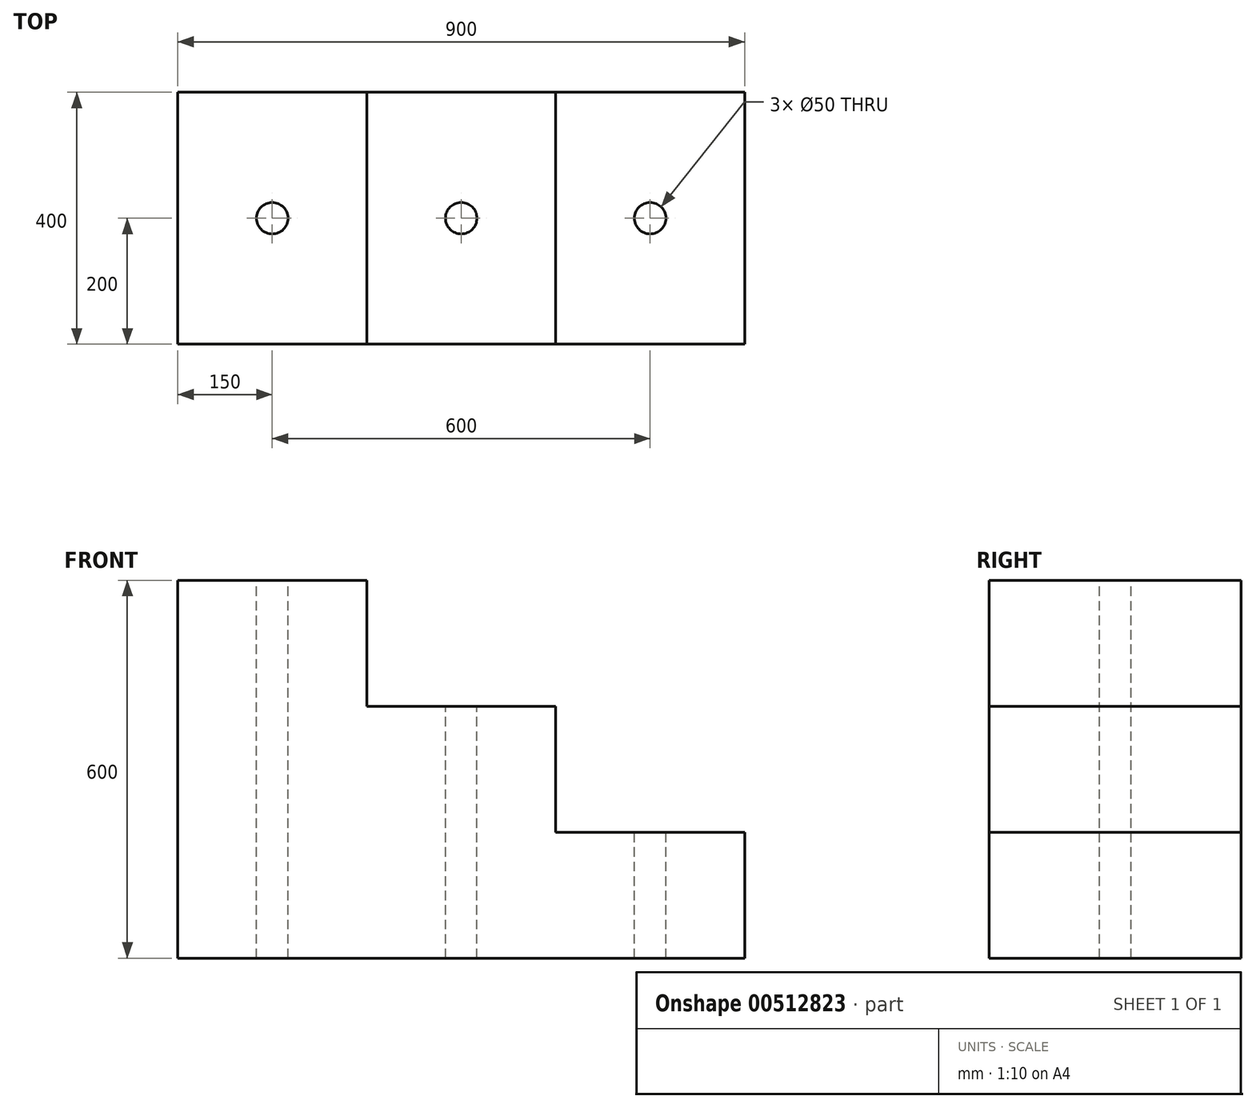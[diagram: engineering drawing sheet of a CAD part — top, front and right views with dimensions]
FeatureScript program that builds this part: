
annotation { "Feature Type Name" : "Feature", "Feature Type Description" : "" }
export const myFeature = defineFeature(function(context is Context, id is Id, definition is map)
    precondition{}
    {
        {
            var Q0;
            Q0=qCreatedBy(makeId("Front.planeOp"),FACE);
            var sketch = newSketch(context, id + "F0", { "sketchPlane" : qUnion([Q0])});
            skLineSegment(sketch, "E0.bottom", {"start": v(-450, 300) * mm, "end": v(-150, 300) * mm});
            skLineSegment(sketch, "E0.top", {"start": v(-450, -300) * mm, "end": v(450, -300) * mm});
            skLineSegment(sketch, "E0.left", {"start": v(-450, 300) * mm, "end": v(-450, -300) * mm});
            skLineSegment(sketch, "E0.right", {"start": v(450, -100) * mm, "end": v(450, -300) * mm});
            skPoint(sketch, "E0.middle", {"position": v(0, 0) * mm});
            skLineSegment(sketch, "E1", {"start": v(-150, 300) * mm, "end": v(-150, 100) * mm});
            skLineSegment(sketch, "E2", {"start": v(-150, 100) * mm, "end": v(150, 100) * mm});
            skPoint(sketch, "E3.end.orphan", {"position": v(150, 0) * mm});
            skLineSegment(sketch, "E4", {"start": v(150, 100) * mm, "end": v(150, -100) * mm});
            skLineSegment(sketch, "E5", {"start": v(150, -100) * mm, "end": v(450, -100) * mm});
            skPoint(sketch, "E6.orphan", {"position": v(450, 300) * mm});
            skSolve(sketch);
        }
        {
            var Q0;
            Q0=makeQuery(id+"F0.imprint","IMPRINT",FACE,{"disambiguationData":[TD([[makeQuery(id+"F0.imprint","IMPRINT",EDGE,{"derivedFrom":sQuery(id+"F0.wireOp",EDGE,"E0.top")}),1.0]])]});
            extrude(context, id + "F1", {"entities" : qUnion([Q0]), "depth" : 400 * mm});
        }
        {
            var Q0;
            Q0=makeQuery(id+"F1.opExtrude","SWEPT_FACE",FACE,{"disambiguationData":[OSD([sQuery(id+"F0.wireOp",EDGE,"E0.bottom")])]});
            var sketch = newSketch(context, id + "F2", { "sketchPlane" : qUnion([Q0])});
            skCircle(sketch, "E7", {"center": v(-300, -200) * mm, "radius": 25 * mm});
            skPoint(sketch, "E7.first.point", {"position": v(-279.89, -214.85) * mm});
            skPoint(sketch, "E7.second.point", {"position": v(-275.67, -194.24) * mm});
            skPoint(sketch, "E7.third.point", {"position": v(-298.62, -175.04) * mm});
            skCircle(sketch, "E8", {"center": v(0, -200) * mm, "radius": 25 * mm});
            skPoint(sketch, "E8.first.point", {"position": v(-5.35, -175.58) * mm});
            skPoint(sketch, "E8.second.point", {"position": v(9.43, -176.85) * mm});
            skPoint(sketch, "E8.third.point", {"position": v(24.24, -193.9) * mm});
            skCircle(sketch, "E9", {"center": v(300, -200) * mm, "radius": 25 * mm});
            skPoint(sketch, "E9.first.point", {"position": v(277.16, -210.17) * mm});
            skPoint(sketch, "E9.second.point", {"position": v(324.7, -196.12) * mm});
            skPoint(sketch, "E9.third.point", {"position": v(285.87, -179.38) * mm});
            skSolve(sketch);
        }
        {
            var Q0;
            Q0=makeQuery(id+"F2.imprint","IMPRINT",FACE,{"disambiguationData":[TD([[makeQuery(id+"F2.imprint","IMPRINT",EDGE,{"derivedFrom":sQuery(id+"F2.wireOp",EDGE,"E7")}),1.0]])]});
            var Q1;
            Q1=makeQuery(id+"F2.imprint","IMPRINT",FACE,{"disambiguationData":[TD([[makeQuery(id+"F2.imprint","IMPRINT",EDGE,{"derivedFrom":sQuery(id+"F2.wireOp",EDGE,"E8")}),1.0]])]});
            var Q2;
            Q2=makeQuery(id+"F2.imprint","IMPRINT",FACE,{"disambiguationData":[TD([[makeQuery(id+"F2.imprint","IMPRINT",EDGE,{"derivedFrom":sQuery(id+"F2.wireOp",EDGE,"E9")}),1.0]])]});
            extrude(context, id + "F3", {"entities" : qUnion([Q0, Q1, Q2]), "operationType" : NewBodyOperationType.REMOVE, "endBound" : BoundingType.THROUGH_ALL, "oppositeDirection" : true, "depth" : 25 * mm});
        }
    });
